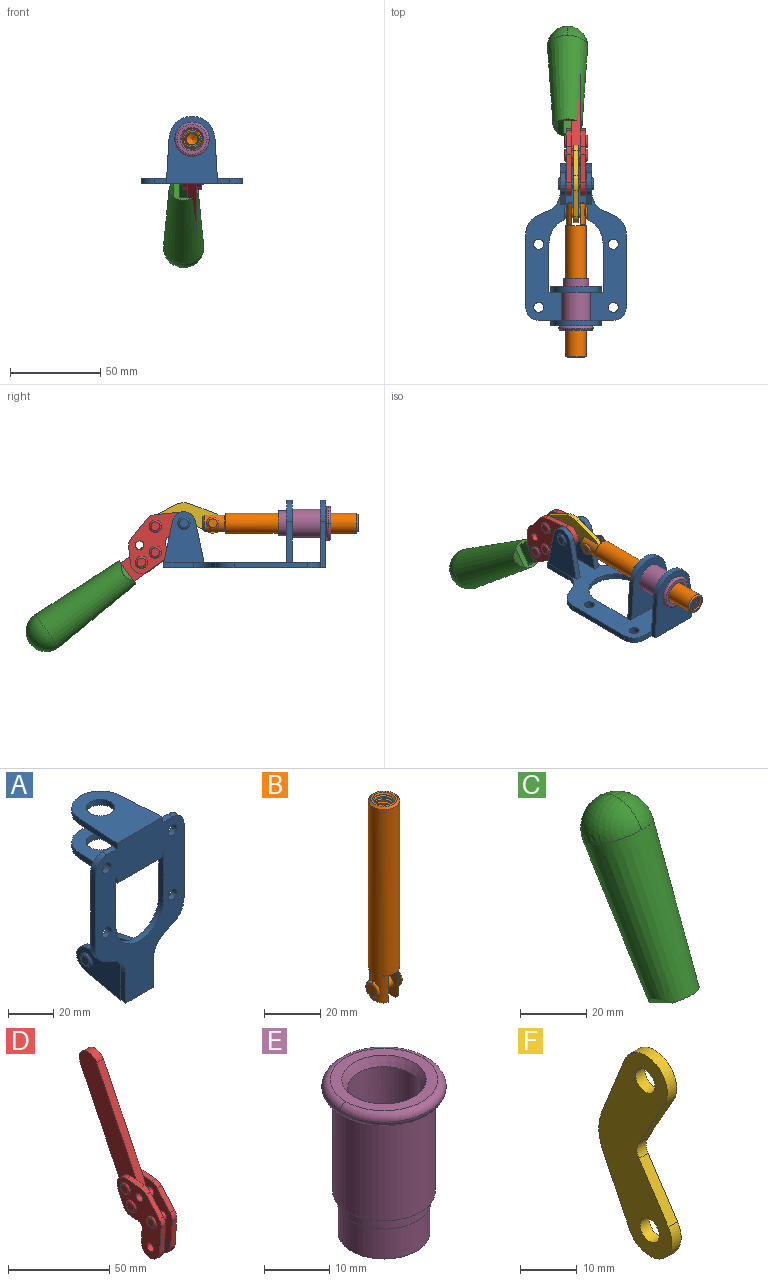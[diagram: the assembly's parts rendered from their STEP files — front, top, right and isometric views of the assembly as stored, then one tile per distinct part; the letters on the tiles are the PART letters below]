
ASSEMBLY  parts=6 mates=6
PART A: 55 faces, bbox 55.7x37.4x89.8 mm
  f0: torus R=2.41mm, axis (-1,0,0), area 15mm2, adj f11,f15,f25
  f1: torus R=2.41mm, axis (-1,0,0), area 15mm2, adj f10,f12,f22
  f2: cylinder r=2.78mm len=5.56mm, axis (0,-1,0), area 54.2mm2, adj f30,f54
  f3: cylinder r=14.99mm len=29.97mm, axis (0,-1,0), area 145.9mm2, adj f30,f49,f53,f54
  f4: cylinder r=2.78mm len=5.56mm, axis (0,-1,0), area 54.2mm2, adj f30,f54
  f5: cylinder r=2.78mm len=5.56mm, axis (0,-1,0), area 54.2mm2, adj f30,f54
  f6: cylinder r=2.78mm len=5.56mm, axis (0,-1,0), area 54.2mm2, adj f30,f54
  f7: cylinder r=6.35mm len=12.7mm, axis (0,0,1), area 123.6mm2, adj f27,f51
  f8: cylinder r=6.35mm len=12.7mm, axis (0,0,-1), area 124.7mm2, adj f21,f35
  f9: cylinder r=2.41mm len=11.18mm, axis (-1,0,0), area 169.4mm2, adj f16,f19
  f10: plane 4.83x4.83mm, normal (1,0,0), area 18.3mm2, adj f1,f12
  f11: plane 4.83x4.83mm, normal (-1,0,0), area 18.3mm2, adj f0,f15
  f12: torus R=2.41mm, axis (-1,0,0), area 15mm2, adj f1,f10,f22
  f13: cylinder r=6.35mm len=12.41mm, axis (1,0,0), area 53.4mm2, adj f18,f19,f22,f23
  f14: cylinder r=6.35mm len=12.41mm, axis (-1,0,0), area 53.4mm2, adj f16,f17,f24,f25
  f15: torus R=2.41mm, axis (-1,0,0), area 15mm2, adj f0,f11,f25
  f16: plane 27.86x22.35mm, normal (1,0,0), area 425.4mm2, adj f9,f14,f17,f24,f30
  f17: plane 22.86x4.97mm, normal (0,0.21,0.98), area 72.5mm2, adj f14,f16,f25,f30
  f18: plane 22.86x4.97mm, normal (0,0.21,0.98), area 72.5mm2, adj f13,f19,f22,f30
  f19: plane 27.86x22.35mm, normal (-1,0,0), area 425.4mm2, adj f9,f13,f18,f23,f30
  f20: cylinder r=12.7mm len=25.35mm, axis (0,0,-1), area 119.8mm2, adj f21,f34,f35,f36
  f21: plane 34.21x28.07mm, normal (0,0,-1), area 702.4mm2, adj f8,f20,f30,f34,f36
  f22: plane 27.96x22.45mm, normal (1,0,0), area 407.2mm2, adj f1,f12,f13,f18,f23,f30,f42,f43
  f23: plane 22.86x4.97mm, normal (0,0.21,-0.98), area 72.5mm2, adj f13,f19,f22,f44
  f24: plane 22.86x4.97mm, normal (0,0.21,-0.98), area 72.5mm2, adj f14,f16,f25,f44
  f25: plane 27.86x22.35mm, normal (-1,0,0), area 407.1mm2, adj f0,f14,f15,f17,f24,f30,f45,f46
  f26: plane 3.1x0.95mm, normal (0,0,-1), area 2.7mm2, adj f30,f49,f50,f54
  f27: plane 34.21x28.07mm, normal (0,0,1), area 702.4mm2, adj f7,f28,f30,f50,f52
  f28: cylinder r=12.7mm len=25.35mm, axis (0,0,1), area 118.8mm2, adj f27,f50,f51,f52
  f29: plane 3.1x0.95mm, normal (0,0,-1), area 2.7mm2, adj f30,f52,f53,f54
  f30: plane 86.54x55.63mm, normal (0,1,0), area 2362.9mm2, adj f2,f3,f4,f5,f6,f16,f17,f18
  f31: plane 40.56x3.1mm, normal (-1,0,0), area 125.7mm2, adj f30,f32,f48,f54
  f32: cylinder r=7.11mm len=7.11mm, axis (0,-1,0), area 34.6mm2, adj f30,f31,f33,f54
  f33: plane 6.67x3.1mm, normal (0,0,1), area 20.4mm2, adj f30,f32,f34,f54
  f34: plane 25.39x3.13mm, normal (-1,0.06,0), area 79.5mm2, adj f20,f21,f33,f35,f54
  f35: plane 37.31x28.45mm, normal (0,0,1), area 789.9mm2, adj f8,f20,f34,f36,f54
  f36: plane 25.39x3.13mm, normal (1,0.06,0), area 79.5mm2, adj f20,f21,f35,f37,f54
  f37: plane 6.67x3.1mm, normal (0,0,1), area 20.4mm2, adj f30,f36,f38,f54
  f38: cylinder r=7.11mm len=7.11mm, axis (0,-1,0), area 34.6mm2, adj f30,f37,f39,f54
  f39: plane 40.56x3.1mm, normal (1,0,0), area 125.7mm2, adj f30,f38,f40,f54
  f40: cylinder r=11.18mm len=10.16mm, axis (0,-1,0), area 39.5mm2, adj f30,f39,f41,f54
  f41: plane 6.09x3.1mm, normal (0.42,0,-0.91), area 20.8mm2, adj f30,f40,f42,f54
  f42: cylinder r=11.18mm len=9.41mm, axis (0,-1,0), area 37.2mm2, adj f22,f30,f41,f43,f54
  f43: plane 16.5x3.1mm, normal (1,0,0), area 51.1mm2, adj f22,f42,f44,f54
  f44: plane 17.37x3.1mm, normal (0,0,-1), area 53.8mm2, adj f23,f24,f30,f43,f45,f54
  f45: plane 16.5x3.1mm, normal (-1,0,0), area 51.1mm2, adj f25,f44,f46,f54
  f46: cylinder r=11.18mm len=9.41mm, axis (0,-1,0), area 37.2mm2, adj f25,f30,f45,f47,f54
  f47: plane 6.09x3.1mm, normal (-0.42,0,-0.91), area 20.8mm2, adj f30,f46,f48,f54
  f48: cylinder r=11.18mm len=10.16mm, axis (0,-1,0), area 39.5mm2, adj f30,f31,f47,f54
  f49: plane 26.54x3.1mm, normal (-1,0,0), area 82.3mm2, adj f3,f26,f30,f54
  f50: plane 25.39x3.1mm, normal (1,0.06,0), area 78.8mm2, adj f26,f27,f28,f51,f54
  f51: plane 37.31x28.45mm, normal (0,0,-1), area 789.9mm2, adj f7,f28,f50,f52,f54
  f52: plane 25.39x3.1mm, normal (-1,0.06,0), area 78.8mm2, adj f27,f28,f29,f51,f54
  f53: plane 26.54x3.1mm, normal (1,0,0), area 82.3mm2, adj f3,f29,f30,f54
  f54: plane 89.66x55.63mm, normal (0,-1,0), area 2678.5mm2, adj f2,f3,f4,f5,f6,f26,f29,f31
PART B: 48 faces, bbox 12.6x11.1x86.1 mm
  f0: torus R=2.41mm, axis (-1,0,0), area 15mm2, adj f30,f32,f34
  f1: torus R=2.41mm, axis (-1,0,0), area 15mm2, adj f29,f31,f33
  f2: cylinder r=5.54mm len=72.39mm, axis (0,0,1), area 2518.5mm2, adj f3,f4,f42,f43
  f3: cone r=5.54mm half-angle=45deg, axis (0,0,1), area 7.6mm2, adj f2,f5,f41
  f4: cone r=5.54mm half-angle=45deg, axis (0,0,-1), area 34.9mm2, adj f2,f39
  f5: cylinder r=5.08mm len=11.48mm, axis (0,0,1), area 108.3mm2, adj f3,f7,f8,f41
  f6: cylinder r=2.41mm len=4.83mm, axis (-1,0,0), area 71.2mm2, adj f40,f41
  f7: cylinder r=2.41mm len=4.83mm, axis (-1,0,0), area 7.6mm2, adj f5,f34
  f8: cone r=5.08mm half-angle=45deg, axis (0,0,1), area 10.6mm2, adj f5,f37,f41
  f9: cone r=3.98mm half-angle=45deg, axis (0,0,1), area 17.6mm2, adj f27,f39,f45,f46,f47
  f10: cylinder r=2.41mm len=4.83mm, axis (-1,0,0), area 7.6mm2, adj f33,f38
  f11: cylinder r=3.2mm len=6.4mm, axis (0,0,1), area 78.4mm2, adj f12,f28,f44,f45,f47
  f12: cylinder r=3.2mm len=6.4mm, axis (0,0,1), area 10.5mm2, adj f11,f13,f45,f47
  f13: cylinder r=3.2mm len=6.4mm, axis (0,0,1), area 10.5mm2, adj f12,f14,f45,f47
  f14: cylinder r=3.2mm len=6.4mm, axis (0,0,1), area 10.5mm2, adj f13,f15,f45,f47
  f15: cylinder r=3.2mm len=6.4mm, axis (0,0,1), area 10.5mm2, adj f14,f16,f45,f47
  f16: cylinder r=3.2mm len=6.4mm, axis (0,0,1), area 10.5mm2, adj f15,f17,f45,f47
  f17: cylinder r=3.2mm len=6.4mm, axis (0,0,1), area 10.5mm2, adj f16,f18,f45,f47
  f18: cylinder r=3.2mm len=6.4mm, axis (0,0,1), area 10.5mm2, adj f17,f19,f45,f47
  f19: cylinder r=3.2mm len=6.4mm, axis (0,0,1), area 10.5mm2, adj f18,f20,f45,f47
  f20: cylinder r=3.2mm len=6.4mm, axis (0,0,1), area 10.5mm2, adj f19,f21,f45,f47
  f21: cylinder r=3.2mm len=6.4mm, axis (0,0,1), area 10.5mm2, adj f20,f22,f45,f47
  f22: cylinder r=3.2mm len=6.4mm, axis (0,0,1), area 10.5mm2, adj f21,f23,f45,f47
  f23: cylinder r=3.2mm len=6.4mm, axis (0,0,1), area 10.5mm2, adj f22,f24,f45,f47
  f24: cylinder r=3.2mm len=6.4mm, axis (0,0,1), area 10.5mm2, adj f23,f25,f45,f47
  f25: cylinder r=3.2mm len=6.4mm, axis (0,0,1), area 10.5mm2, adj f24,f26,f45,f47
  f26: cylinder r=3.2mm len=6.4mm, axis (0,0,1), area 10.5mm2, adj f25,f27,f45,f47
  f27: cylinder r=3.2mm len=6.4mm, axis (0,0,1), area 7.4mm2, adj f9,f26,f45,f47
  f28: cone r=3.2mm half-angle=60deg, axis (0,0,1), area 37.2mm2, adj f11
  f29: plane 4.83x4.83mm, normal (-1,0,0), area 18.3mm2, adj f1,f31
  f30: plane 4.83x4.83mm, normal (1,0,0), area 18.3mm2, adj f0,f32
  f31: torus R=2.41mm, axis (-1,0,0), area 15mm2, adj f1,f29,f33
  f32: torus R=2.41mm, axis (-1,0,0), area 15mm2, adj f0,f30,f34
  f33: plane 6.83x6.83mm, normal (1,0,0), area 18.3mm2, adj f1,f10,f31
  f34: plane 6.83x6.83mm, normal (-1,0,0), area 18.3mm2, adj f0,f7,f32
  f35: cone r=5.08mm half-angle=45deg, axis (0,0,1), area 10.6mm2, adj f36,f38,f40
  f36: plane 7.25x1.97mm, normal (0,0,-1), area 10mm2, adj f35,f40
  f37: plane 7.25x1.97mm, normal (0,0,-1), area 10mm2, adj f8,f41
  f38: cylinder r=5.08mm len=11.48mm, axis (0,0,1), area 108.3mm2, adj f10,f35,f40,f42
  f39: plane 9.55x9.55mm, normal (0,0,1), area 22mm2, adj f4,f9
  f40: plane 12.76x10.09mm, normal (1,0,0), area 95.7mm2, adj f6,f35,f36,f38,f42,f43
  f41: plane 12.76x10.09mm, normal (-1,0,0), area 95.7mm2, adj f3,f5,f6,f8,f37,f43
  f42: cone r=5.54mm half-angle=45deg, axis (0,0,1), area 7.6mm2, adj f2,f38,f40
  f43: plane 11.07x4.7mm, normal (0,0,-1), area 50.4mm2, adj f2,f40,f41
  f44: plane 0.89x0.62mm, normal (-1,0,0), area 0.3mm2, adj f11,f45,f46,f47
  f45: bspline ~24.8x7.63mm, area 266.6mm2, adj f9,f11,f12,f13,f14,f15,f16,f17
  f46: bspline ~24.87x7.63mm, area 73.6mm2, adj f9,f44,f45,f47
  f47: bspline ~24.98x7.63mm, area 272.5mm2, adj f9,f11,f12,f13,f14,f15,f16,f17
PART C: 11 faces, bbox 22.3x42.6x64.5 mm
  f0: sphere r=11.13mm, area 411.4mm2, adj f1,f8
  f1: cone r=11.11mm half-angle=3.3deg, axis (0,0.44,0.9), area 3251.8mm2, adj f0,f7,f8,f9,f10
  f2: cylinder r=6.16mm len=11.7mm, axis (1,0,0), area 89.5mm2, adj f3,f4,f5,f6
  f3: plane 60.23x36.75mm, normal (-1,0,0), area 763.6mm2, adj f2,f4,f6,f10
  f4: plane 51.37x25.05mm, normal (0,0.9,-0.44), area 264.2mm2, adj f2,f3,f5,f10
  f5: plane 60.23x36.75mm, normal (1,0,0), area 763.6mm2, adj f2,f4,f6,f10
  f6: plane 51.37x25.05mm, normal (0,-0.9,0.44), area 264.2mm2, adj f2,f3,f5,f10
  f7: plane 9.95x5.95mm, normal (0.71,-0.31,-0.64), area 25.8mm2, adj f1,f10
  f8: sphere r=11.13mm, area 411.4mm2, adj f0,f1
  f9: plane 9.95x5.95mm, normal (-0.71,-0.31,-0.64), area 25.8mm2, adj f1,f10
  f10: plane 14.27x11.38mm, normal (0,-0.44,-0.9), area 106.7mm2, adj f1,f3,f4,f5,f6,f7,f9
PART D: 59 faces, bbox 12.9x60.2x99.6 mm
  f0: torus R=2.39mm, axis (-1,0,0), area 14.9mm2, adj f20,f43,f51
  f1: torus R=2.39mm, axis (-1,0,0), area 14.9mm2, adj f19,f42,f51
  f2: torus R=2.39mm, axis (-1,0,0), area 14.9mm2, adj f18,f35,f51
  f3: torus R=2.39mm, axis (-1,0,0), area 14.9mm2, adj f14,f17,f23
  f4: torus R=2.39mm, axis (-1,0,0), area 14.9mm2, adj f13,f16,f23
  f5: torus R=2.39mm, axis (-1,0,0), area 14.9mm2, adj f12,f15,f23
  f6: cylinder r=2.39mm len=4.78mm, axis (1,0,0), area 46.5mm2, adj f48,f50,f51
  f7: cylinder r=2.39mm len=4.78mm, axis (1,0,0), area 46.5mm2, adj f50,f51
  f8: cylinder r=6.35mm len=12.68mm, axis (1,0,0), area 61.8mm2, adj f38,f39,f50,f51
  f9: cylinder r=2.39mm len=4.78mm, axis (-1,0,0), area 70.5mm2, adj f46,f50
  f10: cylinder r=2.39mm len=4.78mm, axis (-1,0,0), area 46.5mm2, adj f23,f45,f46
  f11: cylinder r=2.39mm len=4.78mm, axis (-1,0,0), area 46.5mm2, adj f23,f46
  f12: plane 4.78x4.78mm, normal (1,0,0), area 17.9mm2, adj f5,f15
  f13: plane 4.78x4.78mm, normal (1,0,0), area 17.9mm2, adj f4,f16
  f14: plane 4.78x4.78mm, normal (1,0,0), area 17.9mm2, adj f3,f17
  f15: torus R=2.39mm, axis (-1,0,0), area 14.9mm2, adj f5,f12,f23
  f16: torus R=2.39mm, axis (-1,0,0), area 14.9mm2, adj f4,f13,f23
  f17: torus R=2.39mm, axis (-1,0,0), area 14.9mm2, adj f3,f14,f23
  f18: plane 4.78x4.78mm, normal (-1,0,0), area 17.9mm2, adj f2,f35
  f19: plane 4.78x4.78mm, normal (-1,0,0), area 17.9mm2, adj f1,f42
  f20: plane 4.78x4.78mm, normal (-1,0,0), area 17.9mm2, adj f0,f43
  f21: plane 2.26x0.2mm, normal (1,0,0), area 0.2mm2, adj f31,f44
  f22: plane 2.26x0.2mm, normal (-1,0,0), area 0.2mm2, adj f41,f44
  f23: plane 39.37x30.77mm, normal (1,0,0), area 565.5mm2, adj f3,f4,f5,f10,f11,f15,f16,f17
  f24: cylinder r=6.1mm len=4.15mm, axis (-1,0,0), area 14.7mm2, adj f23,f25,f32,f46
  f25: plane 10.25x9.01mm, normal (0,-0.75,0.66), area 42.3mm2, adj f23,f24,f26,f46
  f26: cylinder r=6.35mm len=4.64mm, axis (-1,0,0), area 15.6mm2, adj f23,f25,f27,f46
  f27: plane 15.84x3.1mm, normal (0,-1,-0.07), area 49.2mm2, adj f23,f26,f28,f46
  f28: cylinder r=6.35mm len=12.68mm, axis (-1,0,0), area 61.8mm2, adj f23,f27,f29,f46
  f29: plane 8.11x3.1mm, normal (0,1,0.07), area 25.2mm2, adj f23,f28,f30,f46
  f30: cylinder r=3.05mm len=3.25mm, axis (-1,0,0), area 14.8mm2, adj f23,f29,f31,f46
  f31: plane 5.99x3.1mm, normal (0,0.07,-1), area 18.6mm2, adj f21,f23,f30,f44,f46
  f32: plane 9.5x3.1mm, normal (0,-0.07,1), area 29.5mm2, adj f23,f24,f33,f46,f47
  f33: cylinder r=6.1mm len=8.63mm, axis (-1,0,0), area 39.1mm2, adj f23,f32,f34,f47
  f34: plane 8.65x3.96mm, normal (0,0.91,-0.42), area 29.5mm2, adj f23,f33,f44,f47
  f35: torus R=2.39mm, axis (-1,0,0), area 14.9mm2, adj f2,f18,f51
  f36: plane 10.25x9.01mm, normal (0,-0.75,0.66), area 42.3mm2, adj f37,f49,f50,f51
  f37: cylinder r=6.35mm len=4.64mm, axis (1,0,0), area 15.6mm2, adj f36,f38,f50,f51
  f38: plane 15.84x3.1mm, normal (0,-1,-0.07), area 49.2mm2, adj f8,f37,f50,f51
  f39: plane 8.11x3.1mm, normal (0,1,0.07), area 25.2mm2, adj f8,f40,f50,f51
  f40: cylinder r=3.05mm len=3.25mm, axis (1,0,0), area 14.8mm2, adj f39,f41,f50,f51
  f41: plane 5.99x3.1mm, normal (0,0.07,-1), area 18.6mm2, adj f22,f40,f44,f50,f51
  f42: torus R=2.39mm, axis (-1,0,0), area 14.9mm2, adj f1,f19,f51
  f43: torus R=2.39mm, axis (-1,0,0), area 14.9mm2, adj f0,f20,f51
  f44: cylinder r=6.35mm len=12.12mm, axis (-1,0,0), area 128.9mm2, adj f21,f22,f23,f31,f34,f41,f46,f47
  f45: plane 2.65x1.35mm, normal (1,0,0), area 1mm2, adj f10,f55
  f46: plane 39.08x20.42mm, normal (-1,0,0), area 412.5mm2, adj f9,f10,f11,f24,f25,f26,f27,f28
  f47: plane 77.62x39.82mm, normal (1,0,0), area 850mm2, adj f32,f33,f34,f44,f53,f54,f55
  f48: plane 2.65x1.35mm, normal (-1,0,0), area 1mm2, adj f6,f55
  f49: cylinder r=6.1mm len=4.15mm, axis (1,0,0), area 14.7mm2, adj f36,f50,f51,f56
  f50: plane 39.08x20.42mm, normal (1,0,0), area 412.5mm2, adj f6,f7,f8,f9,f36,f37,f38,f39
  f51: plane 39.37x30.77mm, normal (-1,0,0), area 565.5mm2, adj f0,f1,f2,f6,f7,f8,f35,f36
  f52: plane 8.65x3.96mm, normal (0,0.91,-0.42), area 29.5mm2, adj f44,f51,f57,f58
  f53: plane 68.49x33.4mm, normal (0,0.9,-0.44), area 358.1mm2, adj f44,f47,f54,f58
  f54: cylinder r=6.35mm len=12.06mm, axis (1,0,0), area 93.7mm2, adj f47,f53,f55,f58
  f55: plane 68.49x33.4mm, normal (0,-0.9,0.44), area 358.1mm2, adj f44,f45,f46,f47,f48,f50,f54,f58
  f56: plane 9.5x3.1mm, normal (0,-0.07,1), area 29.5mm2, adj f49,f50,f51,f57,f58
  f57: cylinder r=6.1mm len=8.63mm, axis (1,0,0), area 39.1mm2, adj f51,f52,f56,f58
  f58: plane 77.62x39.82mm, normal (-1,0,0), area 850mm2, adj f44,f52,f53,f54,f55,f56,f57
PART E: 15 faces, bbox 20.6x20.6x28.7 mm
  f0: torus R=8.26mm, axis (0,0,1), area 56.8mm2, adj f1,f10,f12
  f1: torus R=8.26mm, axis (0,0,1), area 56.8mm2, adj f0,f6,f13
  f2: cylinder r=5.59mm len=25.91mm, axis (0,0,1), area 909.6mm2, adj f3,f4
  f3: cone r=6.86mm half-angle=45deg, axis (0,0,-1), area 70.2mm2, adj f2,f14
  f4: cone r=6.47mm half-angle=30deg, axis (0,0,1), area 66.7mm2, adj f2,f13
  f5: cylinder r=7.04mm len=14.07mm, axis (0,0,1), area 252.6mm2, adj f11,f14
  f6: torus R=8.26mm, axis (0,0,1), area 56.8mm2, adj f1,f12,f13
  f7: cylinder r=7.16mm len=14.33mm, axis (0,0,1), area 91.5mm2, adj f9,f11
  f8: cylinder r=7.86mm len=18.42mm, axis (0,0,1), area 909.6mm2, adj f9,f10
  f9: plane 15.72x15.72mm, normal (0,0,-1), area 33mm2, adj f7,f8
  f10: plane 16.51x16.51mm, normal (0,0,-1), area 19.9mm2, adj f0,f8,f12
  f11: plane 14.33x14.33mm, normal (0,0,-1), area 5.7mm2, adj f5,f7
  f12: torus R=8.26mm, axis (0,0,1), area 56.8mm2, adj f0,f6,f10
  f13: plane 16.51x16.51mm, normal (0,0,1), area 82.7mm2, adj f1,f4,f6
  f14: plane 14.07x14.07mm, normal (0,0,-1), area 7.8mm2, adj f3,f5
PART F: 12 faces, bbox 2.3x18.2x42.8 mm
  f0: cylinder r=2.4mm len=4.8mm, axis (1,0,0), area 34.9mm2, adj f4,f11
  f1: cylinder r=10.41mm len=8.47mm, axis (1,0,0), area 20.2mm2, adj f4,f9,f10,f11
  f2: cylinder r=3.05mm len=3.16mm, axis (1,0,0), area 7.7mm2, adj f4,f6,f7,f11
  f3: cylinder r=2.4mm len=4.8mm, axis (1,0,0), area 34.9mm2, adj f4,f11
  f4: plane 42.81x18.23mm, normal (-1,0,0), area 414.1mm2, adj f0,f1,f2,f3,f5,f6,f7,f8
  f5: cylinder r=5.54mm len=10.67mm, axis (1,0,0), area 41.8mm2, adj f4,f6,f10,f11
  f6: plane 11.66x6.53mm, normal (0,-0.87,-0.49), area 30.9mm2, adj f2,f4,f5,f11
  f7: plane 11.17x7.33mm, normal (0,-0.84,0.55), area 30.9mm2, adj f2,f4,f8,f11
  f8: cylinder r=5.54mm len=10.51mm, axis (1,0,0), area 41.8mm2, adj f4,f7,f9,f11
  f9: plane 13.67x6.67mm, normal (0,0.9,-0.44), area 35.1mm2, adj f1,f4,f8,f11
  f10: plane 14.1x5.7mm, normal (0,0.93,0.37), area 35.1mm2, adj f1,f4,f5,f11
  f11: plane 42.81x18.23mm, normal (1,0,0), area 414.1mm2, adj f0,f1,f2,f3,f5,f6,f7,f8
PLACE A rot(axis=(1,0,0),90deg) t=(0,9.14,0)mm fixed
PLACE B rot(axis=(1,0,0),90deg) t=(0,40.79,0)mm
PLACE C rot(axis=(-1,0,0),100deg) t=(-4.66,77.11,43.28)mm
PLACE D rot(axis=(-1,0,0),100deg) t=(0,77.11,43.28)mm
PLACE E rot(axis=(1,0,0),90deg) t=(0,9.14,0)mm
PLACE F rot(axis=(1,0,0),89deg) t=(0,40.36,-0.27)mm
MATE revolute F.f3 <-> D.f4  axis (1,0,0) through (0,57.02,22.95)mm
MATE revolute F.f5 <-> B.f6  axis (1,0,0) through (0,25.31,24.61)mm
MATE slider A.f7 <-> B.f2  axis (0,-1,0) through (0,-37.25,24.61)mm
MATE revolute D.f7 <-> A.f0  axis (1,0,0) through (0,41.23,24.61)mm
MATE fastened A.f7 <-> E.f2  axis (0,-1,0) through (0,-37.25,24.61)mm
MATE fastened C.f2 <-> D.f54  axis (-1,0,0) through (-2.35,118.72,-36.19)mm
